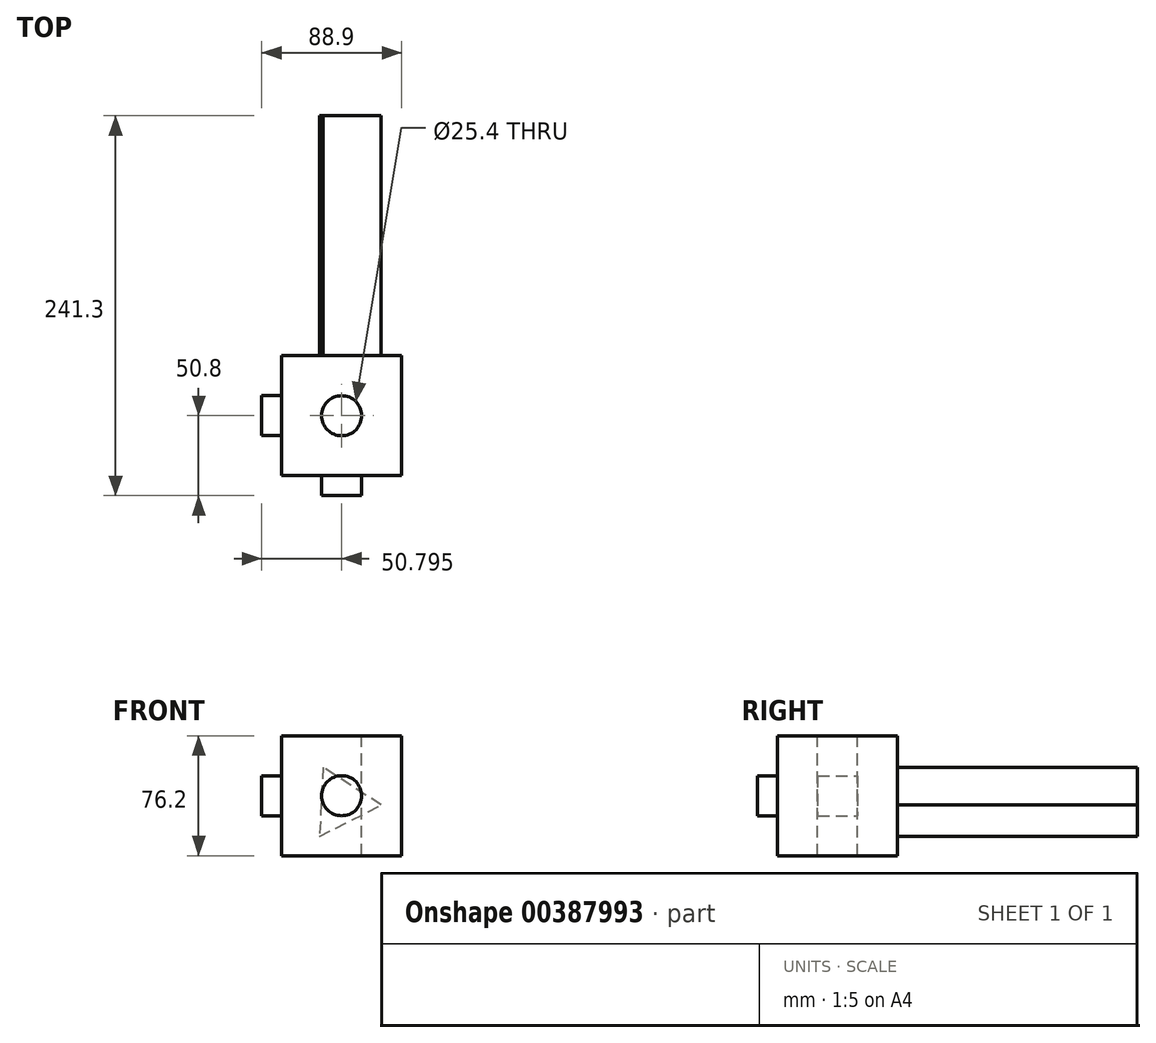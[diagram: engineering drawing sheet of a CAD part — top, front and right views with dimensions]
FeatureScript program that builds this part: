
annotation { "Feature Type Name" : "Feature", "Feature Type Description" : "" }
export const myFeature = defineFeature(function(context is Context, id is Id, definition is map)
    precondition{}
    {
        {
            var Q0;
            Q0=qCreatedBy(makeId("Front.planeOp"),FACE);
            var sketch = newSketch(context, id + "F0", { "sketchPlane" : qUnion([Q0])});
            skLineSegment(sketch, "E0.bottom", {"start": v(-26.53, -18.6) * mm, "end": v(49.67, -18.6) * mm});
            skLineSegment(sketch, "E0.top", {"start": v(-26.53, 57.6) * mm, "end": v(49.67, 57.6) * mm});
            skLineSegment(sketch, "E0.left", {"start": v(-26.53, -18.6) * mm, "end": v(-26.53, 57.6) * mm});
            skLineSegment(sketch, "E0.right", {"start": v(49.67, -18.6) * mm, "end": v(49.67, 57.6) * mm});
            skSolve(sketch);
        }
        {
            var Q0;
            Q0 = qSketchRegion(id + "F0", true);
            extrude(context, id + "F1", {"entities" : qUnion([Q0]), "depth" : 76.2 * mm});
        }
        {
            var Q0;
            Q0=makeQuery(id+"F1.opExtrude","SWEPT_FACE",FACE,{"disambiguationData":[OSD([sQuery(id+"F0.wireOp",EDGE,"E0.top")])]});
            var sketch = newSketch(context, id + "F2", { "sketchPlane" : qUnion([Q0])});
            skPoint(sketch, "E1", {"position": v(11.57, -38.1) * mm});
            skSolve(sketch);
        }
        {
            var Q0;
            Q0=sQuery(id+"F2.wireOp",VERTEX,"E1");
            var Q1;
            Q1=makeQuery(id+"F1.opExtrude","SWEPT_BODY",BODY,{"disambiguationData":[OSD([sQuery(id+"F0.wireOp",EDGE,"E0.bottom"),sQuery(id+"F0.wireOp",EDGE,"E0.top"),sQuery(id+"F0.wireOp",EDGE,"E0.left"),sQuery(id+"F0.wireOp",EDGE,"E0.right")])]});
            hole(context, id + "F3", {"style" : HoleStyle.SIMPLE, "endStyle" : HoleEndStyle.THROUGH, "holeDiameter" : 25.4 * mm, "isTappedThrough" : true, "tappedDepth" : 12.7 * mm, "tapClearance" : 3, "locations" : qUnion([Q0]), "scope" : qUnion([Q1])});
        }
        {
            var Q0;
            Q0=makeQuery(id+"F1.opExtrude","SWEPT_FACE",FACE,{"disambiguationData":[OSD([sQuery(id+"F0.wireOp",EDGE,"E0.left")])]});
            var sketch = newSketch(context, id + "F4", { "sketchPlane" : qUnion([Q0])});
            skLineSegment(sketch, "E2.bottom", {"start": v(50.8, 32.2) * mm, "end": v(25.4, 32.2) * mm});
            skLineSegment(sketch, "E2.top", {"start": v(50.8, 6.8) * mm, "end": v(25.4, 6.8) * mm});
            skLineSegment(sketch, "E2.left", {"start": v(50.8, 32.2) * mm, "end": v(50.8, 6.8) * mm});
            skLineSegment(sketch, "E2.right", {"start": v(25.4, 32.2) * mm, "end": v(25.4, 6.8) * mm});
            skPoint(sketch, "E3", {"position": v(50.8, 32.2) * mm});
            skSolve(sketch);
        }
        {
            var Q0;
            Q0 = qSketchRegion(id + "F4", true);
            extrude(context, id + "F5", {"entities" : qUnion([Q0]), "operationType" : NewBodyOperationType.ADD, "depth" : 12.7 * mm});
        }
        {
            var Q0;
            Q0=makeQuery(id+"F1.opExtrude","CAP_FACE",FACE,{"disambiguationData":[OSD([sQuery(id+"F0.wireOp",EDGE,"E0.bottom"),sQuery(id+"F0.wireOp",EDGE,"E0.top"),sQuery(id+"F0.wireOp",EDGE,"E0.left"),sQuery(id+"F0.wireOp",EDGE,"E0.right")])],"isStart":false});
            var sketch = newSketch(context, id + "F6", { "sketchPlane" : qUnion([Q0])});
            skCircle(sketch, "E4", {"center": v(11.57, 19.5) * mm, "radius": 12.7 * mm});
            skSolve(sketch);
        }
        {
            var Q0;
            Q0=makeQuery(id+"F6.imprint","IMPRINT",FACE,{"disambiguationData":[TD([[makeQuery(id+"F6.imprint","IMPRINT",EDGE,{"derivedFrom":sQuery(id+"F6.wireOp",EDGE,"E4")}),1.0]])]});
            extrude(context, id + "F7", {"entities" : qUnion([Q0]), "operationType" : NewBodyOperationType.ADD, "depth" : 12.7 * mm});
        }
        {
            var Q0;
            Q0=makeQuery(id+"F1.opExtrude","CAP_FACE",FACE,{"disambiguationData":[OSD([sQuery(id+"F0.wireOp",EDGE,"E0.bottom"),sQuery(id+"F0.wireOp",EDGE,"E0.top"),sQuery(id+"F0.wireOp",EDGE,"E0.left"),sQuery(id+"F0.wireOp",EDGE,"E0.right")])],"isStart":true});
            var sketch = newSketch(context, id + "F8", { "sketchPlane" : qUnion([Q0])});
            skCircle(sketch, "E5.cCircle", {"center": v(-11.33, 14.9) * mm, "radius": 12.7 * mm, "construction": true});
            skLineSegment(sketch, "E5.0", {"start": v(-36.7, 13.58) * mm, "end": v(0.2, 37.54) * mm});
            skLineSegment(sketch, "E5.1", {"start": v(0.2, 37.54) * mm, "end": v(2.5, -6.4) * mm});
            skLineSegment(sketch, "E5.2", {"start": v(2.5, -6.4) * mm, "end": v(-36.7, 13.58) * mm});
            skPoint(sketch, "E5.0.midPoint", {"position": v(-18.24, 25.56) * mm});
            skSolve(sketch);
        }
        {
            var Q0;
            Q0=makeQuery(id+"F8.imprint","IMPRINT",FACE,{"disambiguationData":[TD([[makeQuery(id+"F8.imprint","IMPRINT",EDGE,{"derivedFrom":sQuery(id+"F8.wireOp",EDGE,"E5.0")}),-1.0]])]});
            extrude(context, id + "F9", {"entities" : qUnion([Q0]), "operationType" : NewBodyOperationType.ADD, "depth" : 152.4 * mm});
        }
    });
